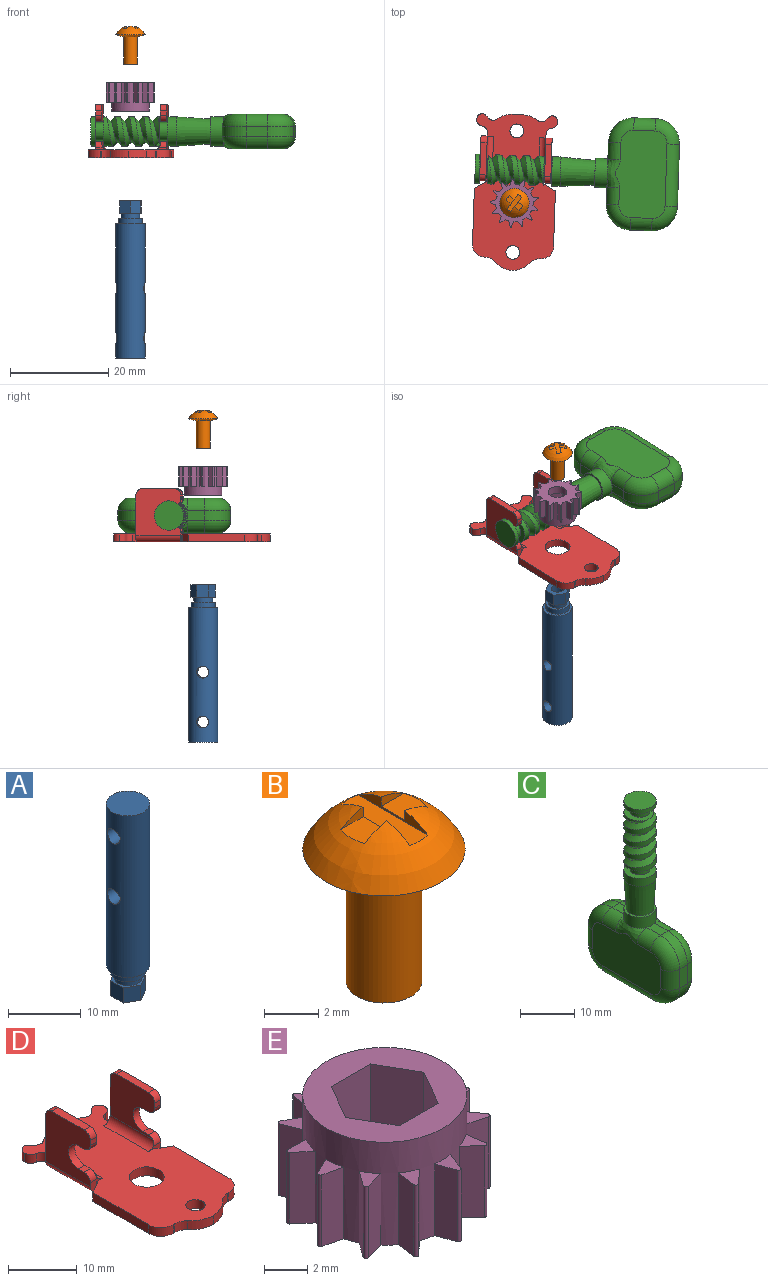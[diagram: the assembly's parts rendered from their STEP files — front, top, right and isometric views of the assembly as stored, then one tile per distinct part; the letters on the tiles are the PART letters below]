
ASSEMBLY  parts=5 mates=4
PART A: 18 faces, bbox 6x6x32 mm
  f0: plane 4.83x4.83mm, normal (0,0,-1), area 6.9mm2, adj f2,f11
  f1: plane 4.99x4.32mm, normal (0,0,1), area 4.7mm2, adj f2,f4,f5,f6,f7,f8,f9
  f2: cylinder r=1.91mm len=3.81mm, axis (0,0,-1), area 12.2mm2, adj f0,f1
  f3: plane 4.99x4.32mm, normal (0,0,-1), area 11.1mm2, adj f4,f5,f6,f7,f8,f9,f14
  f4: plane 2.54x2.16mm, normal (0.5,-0.87,0), area 6.3mm2, adj f1,f3,f5,f9
  f5: plane 2.54x2.16mm, normal (-0.5,-0.87,0), area 6.3mm2, adj f1,f3,f4,f6
  f6: plane 2.54x2.49mm, normal (-1,0,0), area 6.3mm2, adj f1,f3,f5,f7
  f7: plane 2.54x2.16mm, normal (-0.5,0.87,0), area 6.3mm2, adj f1,f3,f6,f8
  f8: plane 2.54x2.16mm, normal (0.5,0.87,0), area 6.3mm2, adj f1,f3,f7,f9
  f9: plane 2.54x2.49mm, normal (1,0,0), area 6.3mm2, adj f1,f3,f4,f8
  f10: plane 5.97x5.97mm, normal (0,0,-1), area 9.7mm2, adj f11,f13
  f11: cylinder r=2.41mm len=4.83mm, axis (0,0,-1), area 17.3mm2, adj f0,f10
  f12: plane 5.97x5.97mm, normal (0,0,1), area 28mm2, adj f13
  f13: cylinder r=2.98mm len=27.31mm, axis (0,0,-1), area 493.4mm2, adj f10,f12,f16,f17
  f14: cylinder r=1.27mm len=5.08mm, axis (0,0,-1), area 40.5mm2, adj f3,f15
  f15: plane 2.54x2.54mm, normal (0,0,-1), area 5.1mm2, adj f14
  f16: cylinder r=1.21mm len=5.97mm, axis (1,0,0), area 43.3mm2, adj f13
  f17: cylinder r=1.21mm len=5.97mm, axis (1,0,0), area 43.3mm2, adj f13
PART B: 13 faces, bbox 6.3x6.3x8.1 mm
  f0: plane 2.79x2.79mm, normal (0,0,-1), area 6.1mm2, adj f1
  f1: cylinder r=1.4mm len=5.59mm, axis (0,0,-1), area 49mm2, adj f0,f2
  f2: cone r=2.98mm half-angle=77.4deg, axis (0,0,1), area 22.4mm2, adj f1,f3
  f3: revolved ~5.97x5.97mm, area 31.2mm2, adj f2,f4,f5,f6,f7,f8,f9,f10
  f4: plane 3.87x0.76mm, normal (1,0,0), area 0.8mm2, adj f3,f5,f10,f11,f12
  f5: plane 3.74x0.93mm, normal (0,0,1), area 3.5mm2, adj f3,f4,f6
  f6: plane 3.87x0.76mm, normal (-1,0,0), area 0.8mm2, adj f3,f5,f7,f8,f9
  f7: plane 1.48x0.74mm, normal (0,-1,0), area 0.3mm2, adj f3,f6,f8
  f8: plane 1.28x1.23mm, normal (0,0,1), area 1.5mm2, adj f3,f6,f7,f9
  f9: plane 1.48x0.74mm, normal (0,1,0), area 0.3mm2, adj f3,f6,f8
  f10: plane 1.48x0.75mm, normal (0,1,0), area 0.3mm2, adj f3,f4,f11
  f11: plane 1.28x1.23mm, normal (0,0,1), area 1.5mm2, adj f3,f4,f10,f12
  f12: plane 1.48x0.75mm, normal (0,-1,0), area 0.3mm2, adj f3,f4,f11
PART C: 48 faces, bbox 7.6x24.1x42.3 mm
  f0: plane 3.54x2.03mm, normal (0,0,1), area 7mm2, adj f13,f23,f31,f42
  f1: cylinder r=2.98mm len=11.43mm, axis (0,0,1), area 84mm2, adj f2,f8,f24,f25,f26,f27
  f2: plane 6.42x6.28mm, normal (0,0,1), area 14.9mm2, adj f1,f9,f24,f25
  f3: plane 5.97x5.97mm, normal (0,0,1), area 7.7mm2, adj f4,f13
  f4: cone r=2.54mm half-angle=3.6deg, axis (0,0,1), area 121.5mm2, adj f3,f5
  f5: cylinder r=2.98mm len=5.97mm, axis (0,0,1), area 33.3mm2, adj f4,f6
  f6: plane 5.97x5.97mm, normal (0,0,1), area 17.3mm2, adj f5,f7
  f7: cylinder r=1.84mm len=3.68mm, axis (0,0,1), area 19.1mm2, adj f6,f8
  f8: plane 6.42x6.28mm, normal (0,0,-1), area 14.9mm2, adj f1,f7,f26,f27
  f9: cylinder r=1.84mm len=3.68mm, axis (0,0,1), area 19.1mm2, adj f2,f10
  f10: plane 5.97x5.97mm, normal (0,0,-1), area 17.3mm2, adj f9,f11
  f11: cylinder r=2.98mm len=5.97mm, axis (0,0,1), area 16.7mm2, adj f10,f12
  f12: plane 5.97x5.97mm, normal (0,0,1), area 28mm2, adj f11
  f13: cylinder r=2.98mm len=5.97mm, axis (0,0,1), area 47.6mm2, adj f0,f3,f17,f29,f40
  f14: plane 4.32x2.03mm, normal (0,-1,0), area 8.8mm2, adj f20,f23,f35,f46
  f15: plane 12.7x2.03mm, normal (0,0,-1), area 25.8mm2, adj f20,f21,f36,f45
  f16: plane 4.32x2.03mm, normal (0,1,0), area 8.8mm2, adj f21,f22,f32,f41
  f17: plane 3.54x2.03mm, normal (0,0,1), area 7mm2, adj f13,f22,f28,f38
  f18: plane 17.78x10.33mm, normal (1,0,0), area 163.8mm2, adj f28,f29,f30,f31,f32,f33,f34,f35
  f19: plane 17.78x10.33mm, normal (-1,0,0), area 163.8mm2, adj f38,f39,f40,f41,f42,f43,f44,f45
  f20: cylinder r=5.08mm len=5.08mm, axis (-1,0,0), area 16.2mm2, adj f14,f15,f37,f47
  f21: cylinder r=5.08mm len=5.08mm, axis (1,0,0), area 16.2mm2, adj f15,f16,f34,f43
  f22: cylinder r=5.08mm len=5.08mm, axis (-1,0,0), area 16.2mm2, adj f16,f17,f30,f39
  f23: cylinder r=5.08mm len=5.08mm, axis (1,0,0), area 16.2mm2, adj f0,f14,f33,f44
  f24: bspline ~12.33x6.89mm, area 78.3mm2, adj f1,f2,f26,f27
  f25: plane 0.9x0.9mm, normal (0,-1,0), area 0.4mm2, adj f1,f2,f27
  f26: plane 0.9x0.9mm, normal (0,1,0), area 0.4mm2, adj f1,f8,f24
  f27: bspline ~12.33x6.89mm, area 78.3mm2, adj f1,f8,f24,f25
  f28: cylinder r=2.54mm len=3.54mm, axis (0,1,0), area 14.1mm2, adj f17,f18,f29,f30
  f29: bspline ~6.22x2.66mm, area 14.5mm2, adj f13,f18,f28,f31
  f30: torus R=2.54mm, axis (1,0,0), area 26.1mm2, adj f18,f22,f28,f32
  f31: cylinder r=2.54mm len=3.54mm, axis (0,1,0), area 14.1mm2, adj f0,f18,f29,f33
  f32: cylinder r=2.54mm len=4.32mm, axis (0,0,-1), area 17.2mm2, adj f16,f18,f30,f34
  f33: torus R=2.54mm, axis (1,0,0), area 26.1mm2, adj f18,f23,f31,f35
  f34: torus R=2.54mm, axis (1,0,0), area 26.1mm2, adj f18,f21,f32,f36
  f35: cylinder r=2.54mm len=4.32mm, axis (0,0,1), area 17.2mm2, adj f14,f18,f33,f37
  f36: cylinder r=2.54mm len=12.7mm, axis (0,-1,0), area 50.7mm2, adj f15,f18,f34,f37
  f37: torus R=2.54mm, axis (1,0,0), area 26.1mm2, adj f18,f20,f35,f36
  f38: cylinder r=2.54mm len=3.54mm, axis (0,-1,0), area 14.1mm2, adj f17,f19,f39,f40
  f39: torus R=2.54mm, axis (1,0,0), area 26.1mm2, adj f19,f22,f38,f41
  f40: bspline ~5.61x2.54mm, area 14.5mm2, adj f13,f19,f38,f42
  f41: cylinder r=2.54mm len=4.32mm, axis (0,0,1), area 17.2mm2, adj f16,f19,f39,f43
  f42: cylinder r=2.54mm len=3.54mm, axis (0,-1,0), area 14.1mm2, adj f0,f19,f40,f44
  f43: torus R=2.54mm, axis (1,0,0), area 26.1mm2, adj f19,f21,f41,f45
  f44: torus R=2.54mm, axis (1,0,0), area 26.1mm2, adj f19,f23,f42,f46
  f45: cylinder r=2.54mm len=12.7mm, axis (0,1,0), area 50.7mm2, adj f15,f19,f43,f47
  f46: cylinder r=2.54mm len=4.32mm, axis (0,0,-1), area 17.2mm2, adj f14,f19,f44,f47
  f47: torus R=2.54mm, axis (1,0,0), area 26.1mm2, adj f19,f20,f45,f46
PART D: 70 faces, bbox 16.5x31.7x10.8 mm
  f0: plane 9.14x7.94mm, normal (-1,0,0), area 55mm2, adj f1,f22,f23,f24,f26,f27,f28,f29
  f1: plane 1.27x0.89mm, normal (0,-1,0), area 1.1mm2, adj f0,f2,f29,f32
  f2: plane 9.53x9.14mm, normal (1,0,0), area 69.5mm2, adj f1,f21,f22,f23,f25,f26,f27,f28
  f3: plane 1.59x0.77mm, normal (1,0,0), area 1.2mm2, adj f4,f6,f11,f22
  f4: plane 31.75x16.51mm, normal (0,0,1), area 376mm2, adj f3,f5,f7,f8,f9,f10,f11,f12
  f5: plane 2.11x1.59mm, normal (0,1,0), area 3.3mm2, adj f4,f6,f13,f43
  f6: plane 31.75x16.51mm, normal (0,0,-1), area 399.2mm2, adj f3,f5,f7,f8,f9,f10,f11,f12
  f7: plane 11.43x1.59mm, normal (1,0,0), area 18.1mm2, adj f4,f6,f9,f19
  f8: plane 1.59x0.01mm, normal (1,0,0), area 0mm2, adj f4,f6,f14,f17
  f9: plane 1.59x0.09mm, normal (0,1,0), area 0.1mm2, adj f4,f6,f7,f20
  f10: plane 1.59x0.25mm, normal (1,0,0), area 0.4mm2, adj f4,f6,f20,f21
  f11: cylinder r=1.27mm len=1.59mm, axis (0,0,-1), area 3mm2, adj f3,f4,f6,f17
  f12: plane 1.59x0.57mm, normal (-0.71,0.71,0), area 1.3mm2, adj f4,f6,f15,f16
  f13: cylinder r=5.08mm len=3.09mm, axis (0,0,-1), area 5.3mm2, adj f4,f5,f6,f16
  f14: cylinder r=1.27mm len=1.59mm, axis (0,0,-1), area 2.9mm2, adj f4,f6,f8,f15
  f15: cylinder r=1.27mm len=1.59mm, axis (0,0,1), area 1.4mm2, adj f4,f6,f12,f14
  f16: cylinder r=1.27mm len=1.67mm, axis (0,0,-1), area 2.9mm2, adj f4,f6,f12,f13
  f17: cylinder r=1.27mm len=1.59mm, axis (0,0,-1), area 3mm2, adj f4,f6,f8,f11
  f18: plane 1.59x0.24mm, normal (0,-1,0), area 0.4mm2, adj f4,f6,f19,f66
  f19: cylinder r=2.54mm len=2.54mm, axis (0,0,1), area 6.3mm2, adj f4,f6,f7,f18
  f20: plane 2.2x1.59mm, normal (0.5,0.87,0), area 4mm2, adj f4,f6,f9,f10
  f21: plane 2.54x2.03mm, normal (0,-1,0), area 2.5mm2, adj f2,f4,f10,f24,f25,f30
  f22: plane 9.53x2.54mm, normal (0,1,0), area 12.1mm2, adj f0,f2,f3,f4,f24,f25,f31
  f23: plane 6.6x1.27mm, normal (0,0,1), area 8.4mm2, adj f0,f2,f31,f32
  f24: cylinder r=1.27mm len=9.14mm, axis (0,-1,0), area 18.2mm2, adj f0,f4,f21,f22,f30
  f25: cylinder r=1.27mm len=9.14mm, axis (0,1,0), area 18.2mm2, adj f2,f6,f21,f22
  f26: plane 1.27x1.13mm, normal (0,0,-1), area 1.4mm2, adj f0,f2,f28,f29
  f27: plane 1.27x1.13mm, normal (0,0,1), area 1.4mm2, adj f0,f2,f28,f30
  f28: cylinder r=2.03mm len=4.06mm, axis (1,0,0), area 8.1mm2, adj f0,f2,f26,f27
  f29: cylinder r=1.27mm len=1.27mm, axis (1,0,0), area 2.5mm2, adj f0,f1,f2,f26
  f30: cylinder r=1.27mm len=1.58mm, axis (-1,0,0), area 2.6mm2, adj f0,f2,f21,f24,f27
  f31: cylinder r=1.27mm len=1.27mm, axis (1,0,0), area 2.5mm2, adj f0,f2,f22,f23
  f32: cylinder r=1.27mm len=1.27mm, axis (-1,0,0), area 2.5mm2, adj f0,f1,f2,f23
  f33: plane 9.14x7.94mm, normal (1,0,0), area 55mm2, adj f34,f52,f53,f54,f56,f57,f58,f59
  f34: plane 1.27x0.89mm, normal (0,-1,0), area 1.1mm2, adj f33,f35,f59,f62
  f35: plane 9.53x9.14mm, normal (-1,0,0), area 69.5mm2, adj f34,f51,f52,f53,f55,f56,f57,f58
  f36: plane 1.59x0.77mm, normal (-1,0,0), area 1.2mm2, adj f4,f6,f41,f52
  f37: plane 11.43x1.59mm, normal (-1,0,0), area 18.1mm2, adj f4,f6,f39,f49
  f38: plane 1.59x0.01mm, normal (-1,0,0), area 0mm2, adj f4,f6,f44,f47
  f39: plane 1.59x0.09mm, normal (0,1,0), area 0.1mm2, adj f4,f6,f37,f50
  f40: plane 1.59x0.25mm, normal (-1,0,0), area 0.4mm2, adj f4,f6,f50,f51
  f41: cylinder r=1.27mm len=1.59mm, axis (0,0,-1), area 3mm2, adj f4,f6,f36,f47
  f42: plane 1.59x0.57mm, normal (0.71,0.71,0), area 1.3mm2, adj f4,f6,f45,f46
  f43: cylinder r=5.08mm len=3.09mm, axis (0,0,-1), area 5.3mm2, adj f4,f5,f6,f46
  f44: cylinder r=1.27mm len=1.59mm, axis (0,0,-1), area 2.9mm2, adj f4,f6,f38,f45
  f45: cylinder r=1.27mm len=1.59mm, axis (0,0,1), area 1.4mm2, adj f4,f6,f42,f44
  f46: cylinder r=1.27mm len=1.67mm, axis (0,0,-1), area 2.9mm2, adj f4,f6,f42,f43
  f47: cylinder r=1.27mm len=1.59mm, axis (0,0,-1), area 3mm2, adj f4,f6,f38,f41
  f48: plane 1.59x0.24mm, normal (0,-1,0), area 0.4mm2, adj f4,f6,f49,f65
  f49: cylinder r=2.54mm len=2.54mm, axis (0,0,1), area 6.3mm2, adj f4,f6,f37,f48
  f50: plane 2.2x1.59mm, normal (-0.5,0.87,0), area 4mm2, adj f4,f6,f39,f40
  f51: plane 2.54x2.03mm, normal (0,-1,0), area 2.5mm2, adj f4,f35,f40,f54,f55,f60
  f52: plane 9.53x2.54mm, normal (0,1,0), area 12.1mm2, adj f4,f33,f35,f36,f54,f55,f61
  f53: plane 6.6x1.27mm, normal (0,0,1), area 8.4mm2, adj f33,f35,f61,f62
  f54: cylinder r=1.27mm len=9.14mm, axis (0,-1,0), area 18.2mm2, adj f4,f33,f51,f52,f60
  f55: cylinder r=1.27mm len=9.14mm, axis (0,1,0), area 18.2mm2, adj f6,f35,f51,f52
  f56: plane 1.27x1.13mm, normal (0,0,-1), area 1.4mm2, adj f33,f35,f58,f59
  f57: plane 1.27x1.13mm, normal (0,0,1), area 1.4mm2, adj f33,f35,f58,f60
  f58: cylinder r=2.03mm len=4.06mm, axis (-1,0,0), area 8.1mm2, adj f33,f35,f56,f57
  f59: cylinder r=1.27mm len=1.27mm, axis (-1,0,0), area 2.5mm2, adj f33,f34,f35,f56
  f60: cylinder r=1.27mm len=1.58mm, axis (1,0,0), area 2.6mm2, adj f33,f35,f51,f54,f57
  f61: cylinder r=1.27mm len=1.27mm, axis (-1,0,0), area 2.5mm2, adj f33,f35,f52,f53
  f62: cylinder r=1.27mm len=1.27mm, axis (1,0,0), area 2.5mm2, adj f33,f34,f35,f53
  f63: cylinder r=5.08mm len=3.58mm, axis (0,0,1), area 6.5mm2, adj f4,f6,f64,f66
  f64: cylinder r=5.08mm len=3.58mm, axis (0,0,-1), area 6.5mm2, adj f4,f6,f63,f65
  f65: cylinder r=2.54mm len=1.89mm, axis (0,0,-1), area 3.4mm2, adj f4,f6,f48,f64
  f66: cylinder r=2.54mm len=1.89mm, axis (0,0,1), area 3.4mm2, adj f4,f6,f18,f63
  f67: cylinder r=2.54mm len=5.08mm, axis (0,0,1), area 25.3mm2, adj f4,f6
  f68: cylinder r=1.4mm len=2.79mm, axis (0,0,1), area 13.9mm2, adj f4,f6
  f69: cylinder r=1.4mm len=2.79mm, axis (0,0,1), area 13.9mm2, adj f4,f6
PART E: 63 faces, bbox 9.8x9.8x5.8 mm
  f0: cylinder r=1.91mm len=3.81mm, axis (0,0,-1), area 19.8mm2, adj f3,f62
  f1: plane 7.62x7.62mm, normal (0,0,1), area 28.5mm2, adj f2,f56,f57,f58,f59,f60,f61
  f2: cylinder r=3.81mm len=7.62mm, axis (0,0,-1), area 85.5mm2, adj f1,f3,f4,f5,f6,f8,f9,f10
  f3: plane 9.84x9.77mm, normal (0,0,-1), area 43.1mm2, adj f0,f2,f4,f5,f7,f8,f9,f11
  f4: plane 4.06x1.1mm, normal (0.94,-0.34,0), area 4.7mm2, adj f2,f3,f6,f7
  f5: plane 4.06x1.1mm, normal (-0.94,-0.34,0), area 4.7mm2, adj f2,f3,f6,f7
  f6: plane 1.18x1.03mm, normal (0,0,1), area 0.7mm2, adj f2,f4,f5,f7
  f7: cylinder r=0.13mm len=4.06mm, axis (0,0,-1), area 1.3mm2, adj f3,f4,f5,f6
  f8: plane 4.06x1.16mm, normal (0.99,0.14,0), area 4.7mm2, adj f2,f3,f10,f11
  f9: plane 4.06x0.86mm, normal (-0.68,-0.74,0), area 4.7mm2, adj f2,f3,f10,f11
  f10: plane 1.3x1.07mm, normal (0,0,1), area 0.7mm2, adj f2,f8,f9,f11
  f11: cylinder r=0.13mm len=4.06mm, axis (0,0,-1), area 1.3mm2, adj f3,f8,f9,f10
  f12: plane 4.06x0.95mm, normal (0.81,0.58,0), area 4.7mm2, adj f2,f3,f14,f15
  f13: plane 4.06x1.13mm, normal (-0.26,-0.97,0), area 4.7mm2, adj f2,f3,f14,f15
  f14: plane 1.29x1.15mm, normal (0,0,1), area 0.7mm2, adj f2,f12,f13,f15
  f15: cylinder r=0.13mm len=4.06mm, axis (0,0,-1), area 1.3mm2, adj f3,f12,f13,f14
  f16: plane 4.06x1.04mm, normal (0.45,0.89,0), area 4.7mm2, adj f2,f3,f18,f19
  f17: plane 4.06x1.14mm, normal (0.22,-0.98,0), area 4.7mm2, adj f2,f3,f18,f19
  f18: plane 1.24x1.02mm, normal (0,0,1), area 0.7mm2, adj f2,f16,f17,f19
  f19: cylinder r=0.13mm len=4.06mm, axis (0,0,-1), area 1.3mm2, adj f3,f16,f17,f18
  f20: plane 4.06x1.17mm, normal (-0.02,1,0), area 4.7mm2, adj f2,f3,f22,f23
  f21: plane 4.06x0.89mm, normal (0.65,-0.76,0), area 4.7mm2, adj f2,f3,f22,f23
  f22: plane 1.3x0.98mm, normal (0,0,1), area 0.7mm2, adj f2,f20,f21,f23
  f23: cylinder r=0.13mm len=4.06mm, axis (0,0,-1), area 1.3mm2, adj f3,f20,f21,f22
  f24: plane 4.06x1.02mm, normal (-0.48,0.88,0), area 4.7mm2, adj f2,f3,f26,f27
  f25: plane 4.06x1.08mm, normal (0.93,-0.37,0), area 4.7mm2, adj f2,f3,f26,f27
  f26: plane 1.26x1.21mm, normal (0,0,1), area 0.7mm2, adj f2,f24,f25,f27
  f27: cylinder r=0.13mm len=4.06mm, axis (0,0,-1), area 1.3mm2, adj f3,f24,f25,f26
  f28: plane 4.06x0.97mm, normal (-0.83,0.55,0), area 4.7mm2, adj f2,f3,f30,f31
  f29: plane 4.06x1.16mm, normal (0.99,0.1,0), area 4.7mm2, adj f2,f3,f30,f31
  f30: plane 1.27x1mm, normal (0,0,1), area 0.7mm2, adj f2,f28,f29,f31
  f31: cylinder r=0.13mm len=4.06mm, axis (0,0,-1), area 1.3mm2, adj f3,f28,f29,f30
  f32: plane 4.06x1.16mm, normal (-0.99,0.1,0), area 4.7mm2, adj f2,f3,f34,f35
  f33: plane 4.06x0.97mm, normal (0.83,0.55,0), area 4.7mm2, adj f2,f3,f34,f35
  f34: plane 1.27x1mm, normal (0,0,1), area 0.7mm2, adj f2,f32,f33,f35
  f35: cylinder r=0.13mm len=4.06mm, axis (0,0,-1), area 1.3mm2, adj f3,f32,f33,f34
  f36: plane 4.06x1.08mm, normal (-0.93,-0.37,0), area 4.7mm2, adj f2,f3,f38,f39
  f37: plane 4.06x1.02mm, normal (0.48,0.88,0), area 4.7mm2, adj f2,f3,f38,f39
  f38: plane 1.26x1.21mm, normal (0,0,1), area 0.7mm2, adj f2,f36,f37,f39
  f39: cylinder r=0.13mm len=4.06mm, axis (0,0,-1), area 1.3mm2, adj f3,f36,f37,f38
  f40: plane 4.06x0.89mm, normal (-0.65,-0.76,0), area 4.7mm2, adj f2,f3,f42,f43
  f41: plane 4.06x1.17mm, normal (0.02,1,0), area 4.7mm2, adj f2,f3,f42,f43
  f42: plane 1.3x0.98mm, normal (0,0,1), area 0.7mm2, adj f2,f40,f41,f43
  f43: cylinder r=0.13mm len=4.06mm, axis (0,0,-1), area 1.3mm2, adj f3,f40,f41,f42
  f44: plane 4.06x1.14mm, normal (-0.22,-0.98,0), area 4.7mm2, adj f2,f3,f46,f47
  f45: plane 4.06x1.04mm, normal (-0.45,0.89,0), area 4.7mm2, adj f2,f3,f46,f47
  f46: plane 1.24x1.02mm, normal (0,0,1), area 0.7mm2, adj f2,f44,f45,f47
  f47: cylinder r=0.13mm len=4.06mm, axis (0,0,-1), area 1.3mm2, adj f3,f44,f45,f46
  f48: plane 4.06x1.13mm, normal (0.26,-0.97,0), area 4.7mm2, adj f2,f3,f50,f51
  f49: plane 4.06x0.95mm, normal (-0.81,0.58,0), area 4.7mm2, adj f2,f3,f50,f51
  f50: plane 1.29x1.15mm, normal (0,0,1), area 0.7mm2, adj f2,f48,f49,f51
  f51: cylinder r=0.13mm len=4.06mm, axis (0,0,-1), area 1.3mm2, adj f3,f48,f49,f50
  f52: plane 4.06x0.86mm, normal (0.68,-0.74,0), area 4.7mm2, adj f2,f3,f54,f55
  f53: plane 4.06x1.16mm, normal (-0.99,0.14,0), area 4.7mm2, adj f2,f3,f54,f55
  f54: plane 1.3x1.07mm, normal (0,0,1), area 0.7mm2, adj f2,f52,f53,f55
  f55: cylinder r=0.13mm len=4.06mm, axis (0,0,-1), area 1.3mm2, adj f3,f52,f53,f54
  f56: plane 4.19x2.57mm, normal (0,-1,0), area 10.8mm2, adj f1,f57,f61,f62
  f57: plane 4.19x2.22mm, normal (0.87,-0.5,0), area 10.8mm2, adj f1,f56,f58,f62
  f58: plane 4.19x2.22mm, normal (0.87,0.5,0), area 10.8mm2, adj f1,f57,f59,f62
  f59: plane 4.19x2.57mm, normal (0,1,0), area 10.8mm2, adj f1,f58,f60,f62
  f60: plane 4.19x2.22mm, normal (-0.87,0.5,0), area 10.8mm2, adj f1,f59,f61,f62
  f61: plane 4.19x2.22mm, normal (-0.87,-0.5,0), area 10.8mm2, adj f1,f56,f60,f62
  f62: plane 5.13x4.45mm, normal (0,0,1), area 5.7mm2, adj f0,f56,f57,f58,f59,f60,f61
PLACE A rot(axis=(1,-0.02,0),180deg) t=(-85.44,51.28,-4.23)mm
PLACE B rot(axis=(0,0,1),143.1deg) t=(-85.44,51.28,-82.94)mm
PLACE C rot(axis=(-0.71,0.01,0.71),178.7deg) t=(-125.45,59.31,-11.47)mm
PLACE D rot(axis=(0,0,-1),1.9deg) t=(-47.64,13.04,-16.81)mm fixed
PLACE E rot(axis=(-0.32,-0.95,0),180deg) t=(-67.93,25.49,-1.5)mm
MATE cylindrical E.f0 <-> A.f2  axis (0,0,1) through (-85.44,51.28,-4.42)mm
MATE cylindrical B.f1 <-> E.f0  axis (0,0,-1) through (-85.44,51.28,5.04)mm
MATE cylindrical C.f1 <-> D.f28  axis (-1,0.03,0) through (-78.64,57.78,-11.47)mm
MATE cylindrical D.f67 <-> A.f2  axis (0,0,1) through (-85.44,51.28,-16.01)mm
